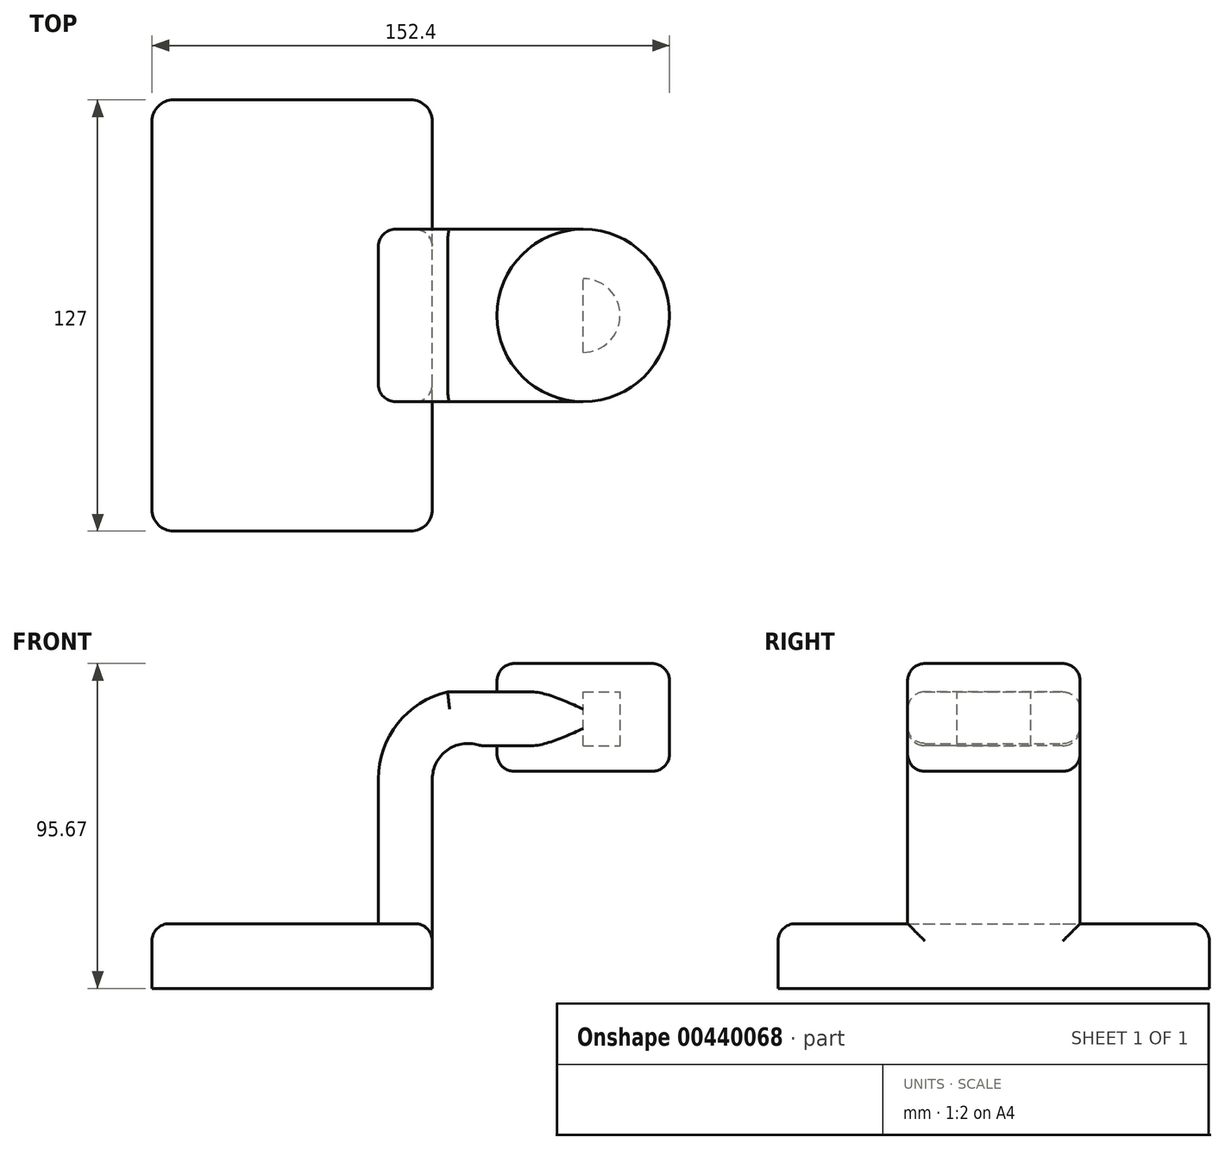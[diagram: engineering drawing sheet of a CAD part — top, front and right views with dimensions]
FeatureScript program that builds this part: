
annotation { "Feature Type Name" : "Feature", "Feature Type Description" : "" }
export const myFeature = defineFeature(function(context is Context, id is Id, definition is map)
    precondition{}
    {
        {
            var Q0;
            Q0=qCreatedBy(makeId("Front.planeOp"),FACE);
            var sketch = newSketch(context, id + "F0", { "sketchPlane" : qUnion([Q0])});
            skLineSegment(sketch, "E0.bottom", {"start": v(41.28, -9.52) * mm, "end": v(-41.28, -9.53) * mm});
            skLineSegment(sketch, "E0.top", {"start": v(41.28, 9.53) * mm, "end": v(-41.28, 9.53) * mm});
            skLineSegment(sketch, "E0.left", {"start": v(41.28, -9.52) * mm, "end": v(41.28, 9.53) * mm});
            skLineSegment(sketch, "E0.right", {"start": v(-41.28, -9.53) * mm, "end": v(-41.28, 9.53) * mm});
            skPoint(sketch, "E0.middle", {"position": v(0, 0) * mm});
            skLineSegment(sketch, "E1.bottom", {"start": v(111.12, 54.39) * mm, "end": v(60.33, 54.39) * mm});
            skLineSegment(sketch, "E1.top", {"start": v(111.13, 86.14) * mm, "end": v(60.33, 86.14) * mm});
            skLineSegment(sketch, "E1.left", {"start": v(111.12, 54.39) * mm, "end": v(111.12, 86.14) * mm});
            skLineSegment(sketch, "E1.right", {"start": v(60.33, 54.39) * mm, "end": v(60.33, 86.14) * mm});
            skPoint(sketch, "E1.middle", {"position": v(85.72, 70.26) * mm});
            skLineSegment(sketch, "E2", {"start": v(41.28, 9.53) * mm, "end": v(41.28, 52.13) * mm});
            skArc(sketch, "E3", {"start": v(41.27, 52.13) * mm, "mid": v(45.81, 60.77) * mm, "end": v(55.5, 61.93) * mm});
            skLineSegment(sketch, "E4", {"start": v(55.5, 61.93) * mm, "end": v(96.57, 61.93) * mm});
            skLineSegment(sketch, "E5.0", {"start": v(45.77, 77.8) * mm, "end": v(96.57, 77.8) * mm});
            skArc(sketch, "E5.1", {"start": v(25.4, 52.13) * mm, "mid": v(31.11, 68.51) * mm, "end": v(45.77, 77.8) * mm});
            skLineSegment(sketch, "E5.2", {"start": v(25.4, 19.18) * mm, "end": v(25.4, 52.13) * mm});
            skLineSegment(sketch, "E6", {"start": v(96.57, 77.8) * mm, "end": v(96.57, 61.93) * mm});
            skFitSpline(sketch, "E7", {"points": [v(-41.28, 9.53) * mm, v(45.77, 77.8) * mm], "startDerivative": vector(2.15, 139.48) * mm, "endDerivative": vector(151.36, 0.64) * mm});
            skLineSegment(sketch, "E8", {"start": v(25.4, 9.53) * mm, "end": v(25.4, 19.18) * mm});
            skLineSegment(sketch, "E9", {"start": v(85.72, 86.14) * mm, "end": v(85.72, 54.39) * mm});
            skSolve(sketch);
        }
        {
            var Q0;
            Q0=makeQuery(id+"F0.imprint","IMPRINT",FACE,{"disambiguationData":[TD([[makeQuery(id+"F0.imprint","IMPRINT",EDGE,{"derivedFrom":sQuery(id+"F0.wireOp",EDGE,"E0.bottom")}),-1.0]])]});
            extrude(context, id + "F1", {"entities" : qUnion([Q0]), "endBound" : BoundingType.SYMMETRIC, "depth" : 127 * mm});
        }
        {
            var Q0;
            {var subQ5=sQuery(id+"F0.wireOp",EDGE,"E2");Q0=makeQuery(id+"F0.imprint","IMPRINT",FACE,{"disambiguationData":[TD([[makeQuery(id+"F0.imprint","IMPRINT",EDGE,{"derivedFrom":subQ5}),1.0]])]});}
            extrude(context, id + "F2", {"entities" : qUnion([Q0]), "operationType" : NewBodyOperationType.ADD, "endBound" : BoundingType.SYMMETRIC, "depth" : 50.8 * mm});
        }
        {
            var Q0;
            Q0=makeQuery(id+"F0.imprint","IMPRINT",FACE,{"disambiguationData":[TD([[makeQuery(id+"F0.imprint","IMPRINT",EDGE,{"derivedFrom":sQuery(id+"F0.wireOp",EDGE,"E5.1")}),1.0]])]});
            extrude(context, id + "F3", {"entities" : qUnion([Q0]), "operationType" : NewBodyOperationType.ADD, "endBound" : BoundingType.SYMMETRIC, "depth" : 15.88 * mm});
        }
        {
            var Q0;
            {var subQ0=sQuery(id+"F0.wireOp",EDGE,"E4");var subQ1=sQuery(id+"F0.wireOp",EDGE,"E1.right");var subQ2=makeQuery(id+"F0.imprint","INTERSECT",VERTEX,{"derivedFrom":[subQ1,subQ0]});Q0=makeQuery(id+"F0.imprint","IMPRINT",FACE,{"disambiguationData":[TD([[makeQuery(id+"F0.imprint","IMPRINT",EDGE,{"disambiguationData":[TD([[subQ2,-1.0]])],"derivedFrom":subQ1}),-1.0]])]});}
            extrude(context, id + "F4", {"entities" : qUnion([Q0]), "operationType" : NewBodyOperationType.ADD, "endBound" : BoundingType.SYMMETRIC, "depth" : 50.8 * mm});
        }
        {
            var Q0;
            {var subQ0=sQuery(id+"F0.wireOp",EDGE,"E1.left");Q0=makeQuery(id+"F0.imprint","IMPRINT",FACE,{"disambiguationData":[TD([[makeQuery(id+"F0.imprint","IMPRINT",EDGE,{"derivedFrom":subQ0}),1.0]])]});}
            var Q1;
            Q1=sQuery(id+"F0.wireOp",EDGE,"E9");
            revolve(context, id + "F5", {"operationType" : NewBodyOperationType.ADD, "entities" : qUnion([Q0]), "axis" : qUnion([Q1]), "revolveType" : RevolveType.FULL});
        }
        {
            var Q0;
            Q0=makeQuery(id+"F1.opExtrude","CAP_EDGE",EDGE,{"disambiguationData":[OSD([sQuery(id+"F0.wireOp",EDGE,"E0.right")])],"isStart":false});
            var Q1;
            Q1=makeQuery(id+"F1.opExtrude","CAP_EDGE",EDGE,{"disambiguationData":[OSD([sQuery(id+"F0.wireOp",EDGE,"E0.left")])],"isStart":false});
            var Q2;
            Q2=makeQuery(id+"F1.opExtrude","CAP_EDGE",EDGE,{"disambiguationData":[OSD([sQuery(id+"F0.wireOp",EDGE,"E0.left")])],"isStart":true});
            var Q3;
            Q3=makeQuery(id+"F1.opExtrude","CAP_EDGE",EDGE,{"disambiguationData":[OSD([sQuery(id+"F0.wireOp",EDGE,"E0.right")])],"isStart":true});
            fillet(context, id + "F6", {"entities" : qUnion([Q0, Q1, Q2, Q3]), "radius" : 6.35 * mm, "tangentPropagation" : true, "allowEdgeOverflow" : false});
        }
        {
            var Q0;
            Q0=makeQuery(id+"F2.opExtrude","CAP_EDGE",EDGE,{"disambiguationData":[OSD([sQuery(id+"F0.wireOp",EDGE,"E5.1")])],"isStart":false});
            var Q1;
            {var subQ0=sQuery(id+"F0.wireOp",EDGE,"E5.0");Q1=makeQuery(id+"F4.boolean.opBoolean","MERGE",EDGE,{"derivedFrom":[makeQuery(id+"F2.opExtrude","CAP_EDGE",EDGE,{"disambiguationData":[OSD([subQ0])],"isStart":false}),makeQuery(id+"F4.opExtrude","CAP_EDGE",EDGE,{"disambiguationData":[OSD([subQ0])],"isStart":false})]});}
            var Q2;
            Q2=makeQuery(id+"F3.opExtrude","CAP_EDGE",EDGE,{"disambiguationData":[OSD([sQuery(id+"F0.wireOp",EDGE,"E7")])],"isStart":false});
            var Q3;
            Q3=makeQuery(id+"F3.opExtrude","CAP_EDGE",EDGE,{"disambiguationData":[OSD([sQuery(id+"F0.wireOp",EDGE,"E7")])],"isStart":true});
            var Q4;
            Q4=makeQuery(id+"F5.opRevolve","SWEPT_EDGE",EDGE,{"disambiguationData":[OSD([sQuery(id+"F0.wireOp",EDGE,"E1.top"),sQuery(id+"F0.wireOp",EDGE,"E1.left")])]});
            var Q5;
            Q5=makeQuery(id+"F2.opExtrude","CAP_EDGE",EDGE,{"disambiguationData":[OSD([sQuery(id+"F0.wireOp",EDGE,"E2")])],"isStart":false});
            var Q6;
            Q6=makeQuery(id+"F2.opExtrude","CAP_EDGE",EDGE,{"disambiguationData":[OSD([sQuery(id+"F0.wireOp",EDGE,"E2")])],"isStart":true});
            var Q7;
            {var subQ0=sQuery(id+"F0.wireOp",EDGE,"E5.0");Q7=makeQuery(id+"F4.boolean.opBoolean","MERGE",EDGE,{"derivedFrom":[makeQuery(id+"F2.opExtrude","CAP_EDGE",EDGE,{"disambiguationData":[OSD([subQ0])],"isStart":true}),makeQuery(id+"F4.opExtrude","CAP_EDGE",EDGE,{"disambiguationData":[OSD([subQ0])],"isStart":true})]});}
            var Q8;
            Q8=makeQuery(id+"F5.opRevolve","SWEPT_EDGE",EDGE,{"disambiguationData":[OSD([sQuery(id+"F0.wireOp",EDGE,"E1.bottom"),sQuery(id+"F0.wireOp",EDGE,"E1.left")])]});
            var Q9;
            {var subQ0=sQuery(id+"F0.wireOp",EDGE,"E7");var subQ1=sQuery(id+"F0.wireOp",EDGE,"E0.top");var subQ2=sQuery(id+"F0.wireOp",EDGE,"E0.right");Q9=makeQuery(id+"F3.boolean.opBoolean","SPLIT",EDGE,{"disambiguationData":[TD([makeQuery(id+"F1.opExtrude","CAP_FACE",FACE,{"disambiguationData":[OSD([sQuery(id+"F0.wireOp",EDGE,"E0.bottom"),subQ1,sQuery(id+"F0.wireOp",EDGE,"E0.left"),subQ2])],"isStart":true})])],"derivedFrom":makeQuery(id+"F1.opExtrude","SWEPT_EDGE",EDGE,{"disambiguationData":[OSD([subQ1,subQ2,subQ0])]})});}
            var Q10;
            Q10=makeQuery(id+"F1.opExtrude","CAP_EDGE",EDGE,{"disambiguationData":[OSD([sQuery(id+"F0.wireOp",EDGE,"E0.top")])],"isStart":true});
            var Q11;
            {var subQ4=sQuery(id+"F0.wireOp",EDGE,"E0.top");var subQ5=sQuery(id+"F0.wireOp",EDGE,"E0.right");var subQ6=sQuery(id+"F0.wireOp",EDGE,"E0.left");Q11=makeQuery(id+"F6.opFillet","BLEND_EDGE",EDGE,{"blendedFrom":[makeQuery(id+"F1.opExtrude","CAP_EDGE",EDGE,{"disambiguationData":[OSD([subQ5])],"isStart":true}),makeQuery(id+"F3.boolean.opBoolean","SPLIT",FACE,{"disambiguationData":[TD([makeQuery(id+"F1.opExtrude","CAP_FACE",FACE,{"disambiguationData":[OSD([sQuery(id+"F0.wireOp",EDGE,"E0.bottom"),subQ4,subQ6,subQ5])],"isStart":true})])],"derivedFrom":makeQuery(id+"F1.opExtrude","SWEPT_FACE",FACE,{"disambiguationData":[OSD([subQ4])]})})],"blendedInto":[makeQuery(id+"F3.boolean.opBoolean","SPLIT",FACE,{"disambiguationData":[TD([makeQuery(id+"F1.opExtrude","CAP_FACE",FACE,{"disambiguationData":[OSD([sQuery(id+"F0.wireOp",EDGE,"E0.bottom"),subQ4,subQ6,subQ5])],"isStart":true})])],"derivedFrom":makeQuery(id+"F1.opExtrude","SWEPT_FACE",FACE,{"disambiguationData":[OSD([subQ4])]})})]});}
            var Q12;
            Q12=makeQuery(id+"F3.opExtrude","CAP_EDGE",EDGE,{"disambiguationData":[OSD([sQuery(id+"F0.wireOp",EDGE,"E0.top")])],"isStart":true});
            var Q13;
            Q13=makeQuery(id+"F3.opExtrude","CAP_EDGE",EDGE,{"disambiguationData":[OSD([sQuery(id+"F0.wireOp",EDGE,"E0.top")])],"isStart":false});
            var Q14;
            {var subQ0=sQuery(id+"F0.wireOp",EDGE,"E7");var subQ1=sQuery(id+"F0.wireOp",EDGE,"E0.top");var subQ2=sQuery(id+"F0.wireOp",EDGE,"E0.right");Q14=makeQuery(id+"F3.boolean.opBoolean","SPLIT",EDGE,{"disambiguationData":[TD([makeQuery(id+"F1.opExtrude","CAP_FACE",FACE,{"disambiguationData":[OSD([sQuery(id+"F0.wireOp",EDGE,"E0.bottom"),subQ1,sQuery(id+"F0.wireOp",EDGE,"E0.left"),subQ2])],"isStart":false})])],"derivedFrom":makeQuery(id+"F1.opExtrude","SWEPT_EDGE",EDGE,{"disambiguationData":[OSD([subQ1,subQ2,subQ0])]})});}
            var Q15;
            Q15=makeQuery(id+"F2.opExtrude","CAP_EDGE",EDGE,{"disambiguationData":[OSD([sQuery(id+"F0.wireOp",EDGE,"E5.1")])],"isStart":true});
            var Q16;
            {var subQ0=sQuery(id+"F0.wireOp",EDGE,"E4");Q16=makeQuery(id+"F4.boolean.opBoolean","MERGE",EDGE,{"derivedFrom":[makeQuery(id+"F2.opExtrude","CAP_EDGE",EDGE,{"disambiguationData":[OSD([subQ0])],"isStart":false}),makeQuery(id+"F4.opExtrude","CAP_EDGE",EDGE,{"disambiguationData":[OSD([subQ0])],"isStart":false})]});}
            var Q17;
            {var subQ0=sQuery(id+"F0.wireOp",EDGE,"E4");Q17=makeQuery(id+"F4.boolean.opBoolean","MERGE",EDGE,{"derivedFrom":[makeQuery(id+"F2.opExtrude","CAP_EDGE",EDGE,{"disambiguationData":[OSD([subQ0])],"isStart":true}),makeQuery(id+"F4.opExtrude","CAP_EDGE",EDGE,{"disambiguationData":[OSD([subQ0])],"isStart":true})]});}
            var Q18;
            Q18=makeQuery(id+"F2.opExtrude","CAP_EDGE",EDGE,{"disambiguationData":[OSD([sQuery(id+"F0.wireOp",EDGE,"E3")])],"isStart":false});
            var Q19;
            Q19=makeQuery(id+"F2.opExtrude","CAP_EDGE",EDGE,{"disambiguationData":[OSD([sQuery(id+"F0.wireOp",EDGE,"E3")])],"isStart":true});
            var Q20;
            Q20=makeQuery(id+"F2.opExtrude","SWEPT_EDGE",EDGE,{"disambiguationData":[OSD([sQuery(id+"F0.wireOp",EDGE,"E3"),sQuery(id+"F0.wireOp",EDGE,"E4")])]});
            var Q21;
            Q21=makeQuery(id+"F4.opExtrude","CAP_EDGE",EDGE,{"disambiguationData":[OSD([sQuery(id+"F0.wireOp",EDGE,"E9")])],"isStart":false});
            var Q22;
            Q22=makeQuery(id+"F4.opExtrude","CAP_EDGE",EDGE,{"disambiguationData":[OSD([sQuery(id+"F0.wireOp",EDGE,"E9")])],"isStart":true});
            fillet(context, id + "F7", {"entities" : qUnion([Q0, Q1, Q2, Q3, Q4, Q5, Q6, Q7, Q8, Q9, Q10, Q11, Q12, Q13, Q14, Q15, Q16, Q17, Q18, Q19, Q20, Q21, Q22]), "radius" : 5.08 * mm, "tangentPropagation" : true, "allowEdgeOverflow" : false});
        }
    });
